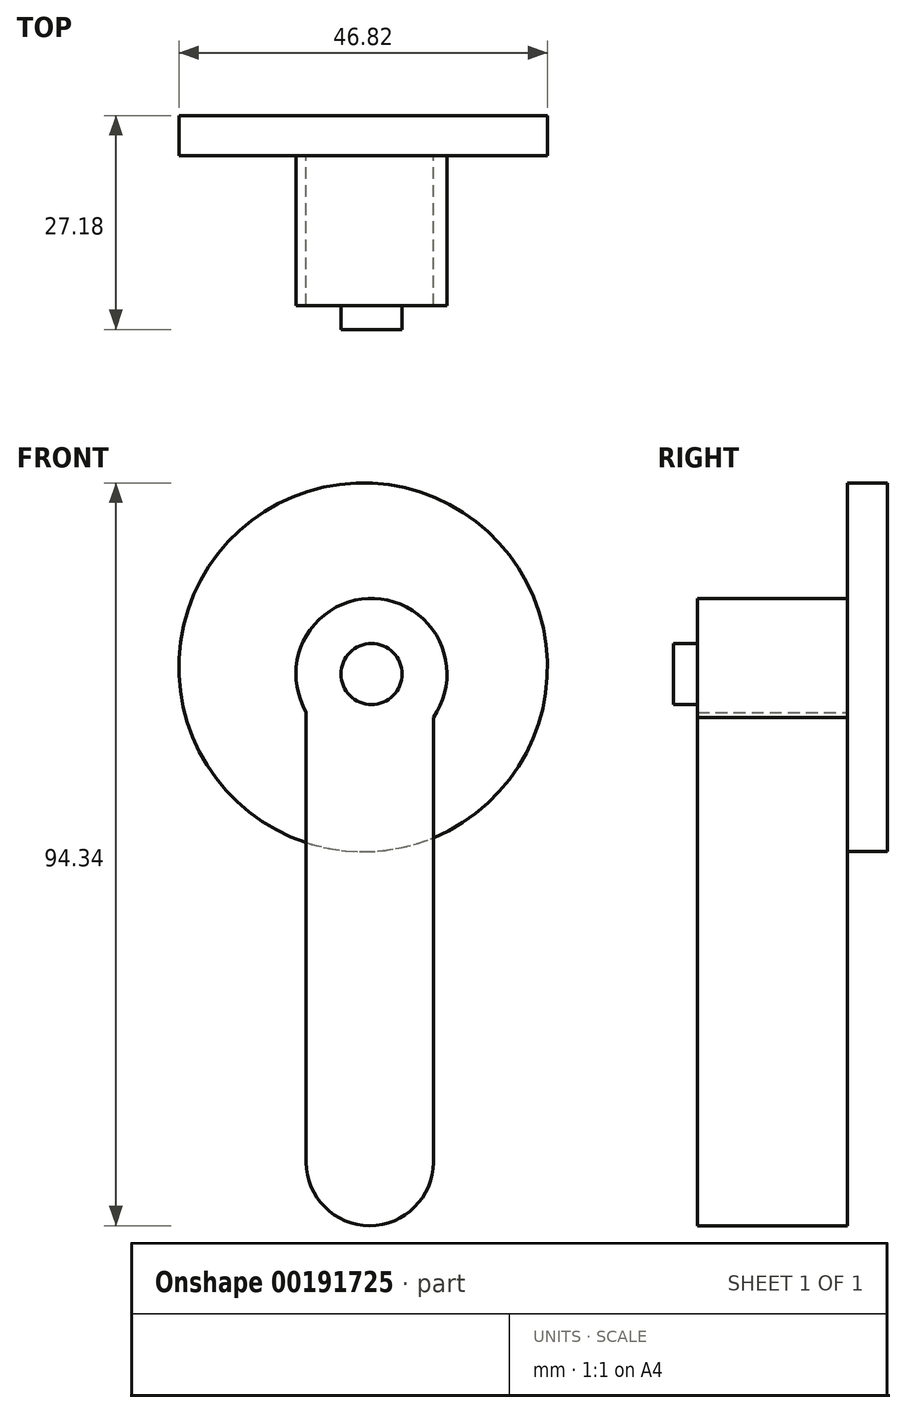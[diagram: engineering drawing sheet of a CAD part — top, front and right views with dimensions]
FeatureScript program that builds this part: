
annotation { "Feature Type Name" : "Feature", "Feature Type Description" : "" }
export const myFeature = defineFeature(function(context is Context, id is Id, definition is map)
    precondition{}
    {
        {
            var Q0;
            Q0=qCreatedBy(makeId("Front.planeOp"),FACE);
            var sketch = newSketch(context, id + "F0", { "sketchPlane" : qUnion([Q0])});
            skCircle(sketch, "E0", {"center": v(0, 0) * mm, "radius": 23.41 * mm});
            skSolve(sketch);
        }
        {
            var Q0;
            Q0 = qSketchRegion(id + "F0", true);
            extrude(context, id + "F1", {"entities" : qUnion([Q0]), "depth" : 5.08 * mm});
        }
        {
            var Q0;
            Q0=makeQuery(id+"F1.opExtrude","CAP_FACE",FACE,{"disambiguationData":[OSD([sQuery(id+"F0.wireOp",EDGE,"E0")])],"isStart":false});
            var sketch = newSketch(context, id + "F2", { "sketchPlane" : qUnion([Q0])});
            skLineSegment(sketch, "E1", {"start": v(-7.23, -5.72) * mm, "end": v(-7.23, -62.86) * mm});
            skLineSegment(sketch, "E2", {"start": v(8.9, -6.39) * mm, "end": v(8.9, -62.86) * mm});
            skArc(sketch, "E3", {"start": v(8.9, -6.39) * mm, "mid": v(1.46, 8.74) * mm, "end": v(-7.23, -5.72) * mm});
            skArc(sketch, "E4", {"start": v(-7.23, -62.86) * mm, "mid": v(0.84, -70.93) * mm, "end": v(8.9, -62.86) * mm});
            skSolve(sketch);
        }
        {
            var Q0;
            {var subQ0=sQuery(id+"F2.wireOp",EDGE,"E4");Q0=makeQuery(id+"F2.imprint","IMPRINT",FACE,{"disambiguationData":[TD([[makeQuery(id+"F2.imprint","IMPRINT",EDGE,{"derivedFrom":subQ0}),1.0]])]});}
            var Q1;
            {var subQ0=sQuery(id+"F2.wireOp",EDGE,"E3");Q1=makeQuery(id+"F2.imprint","IMPRINT",FACE,{"disambiguationData":[TD([[makeQuery(id+"F2.imprint","IMPRINT",EDGE,{"derivedFrom":subQ0}),1.0]])]});}
            extrude(context, id + "F3", {"entities" : qUnion([Q0, Q1]), "operationType" : NewBodyOperationType.ADD, "depth" : 19.05 * mm});
        }
        {
            var Q0;
            Q0=makeQuery(id+"F3.opExtrude","CAP_FACE",FACE,{"disambiguationData":[OSD([sQuery(id+"F2.wireOp",EDGE,"E1"),sQuery(id+"F2.wireOp",EDGE,"E2"),sQuery(id+"F2.wireOp",EDGE,"E3"),sQuery(id+"F2.wireOp",EDGE,"E4")])],"isStart":false});
            var sketch = newSketch(context, id + "F4", { "sketchPlane" : qUnion([Q0])});
            skCircle(sketch, "E5", {"center": v(1.06, -0.85) * mm, "radius": 3.88 * mm});
            skSolve(sketch);
        }
        {
            var Q0;
            Q0=makeQuery(id+"F4.imprint","IMPRINT",FACE,{"disambiguationData":[TD([[makeQuery(id+"F4.imprint","IMPRINT",EDGE,{"derivedFrom":sQuery(id+"F4.wireOp",EDGE,"E5")}),1.0]])]});
            extrude(context, id + "F5", {"entities" : qUnion([Q0]), "operationType" : NewBodyOperationType.ADD, "depth" : 3.05 * mm});
        }
    });
